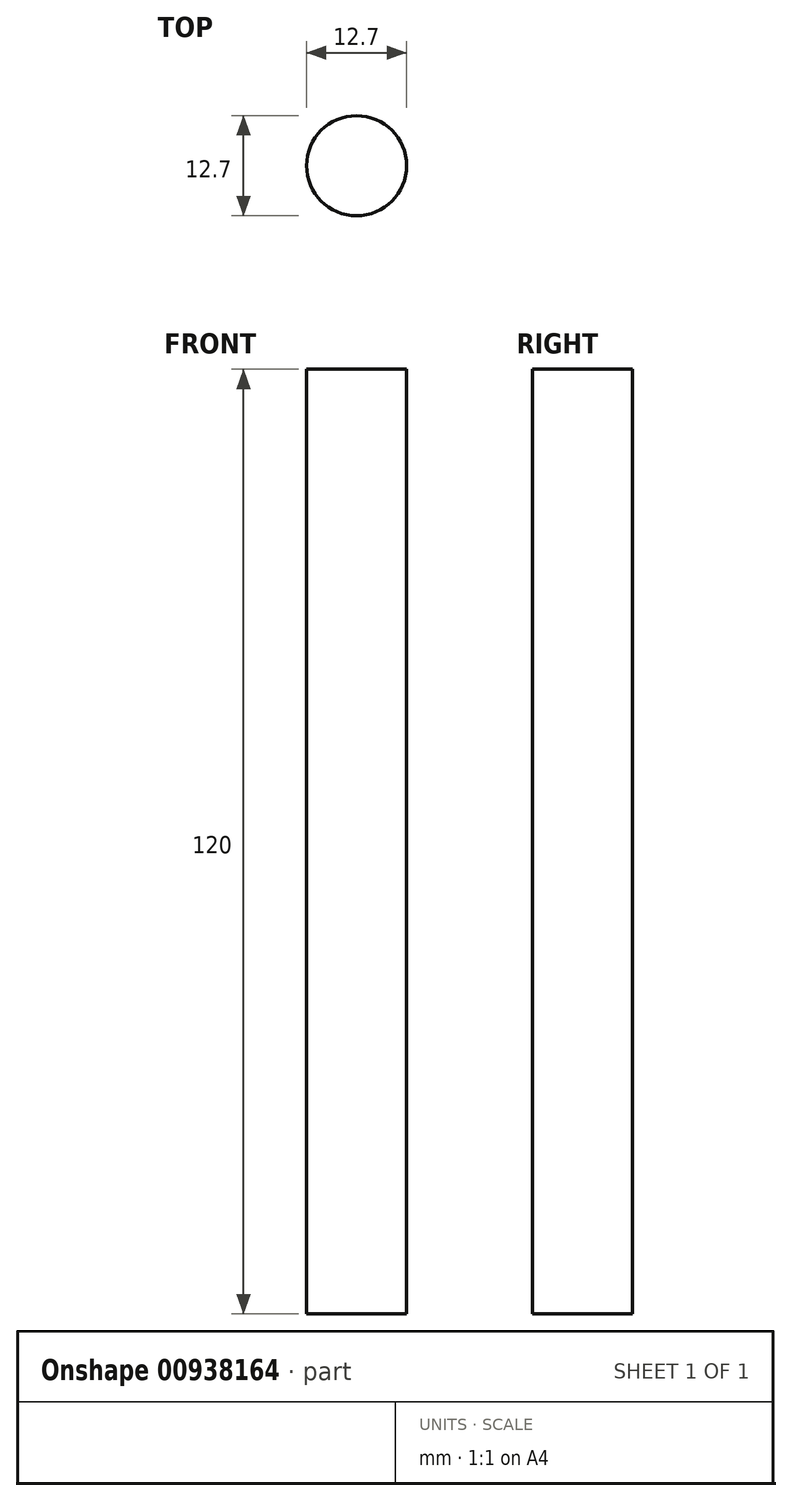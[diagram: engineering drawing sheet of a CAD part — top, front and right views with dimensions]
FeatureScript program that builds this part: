
annotation { "Feature Type Name" : "Feature", "Feature Type Description" : "" }
export const myFeature = defineFeature(function(context is Context, id is Id, definition is map)
    precondition{}
    {
        {
            var Q0;
            Q0=qCreatedBy(makeId("Top.planeOp"),FACE);
            var sketch = newSketch(context, id + "F0", { "sketchPlane" : qUnion([Q0])});
            skCircle(sketch, "E0", {"center": v(11.02, 41.68) * mm, "radius": 6.35 * mm});
            skSolve(sketch);
        }
        {
            var Q0;
            Q0=makeQuery(id+"F0.imprint","IMPRINT",FACE,{"disambiguationData":[TD([[makeQuery(id+"F0.imprint","IMPRINT",EDGE,{"derivedFrom":sQuery(id+"F0.wireOp",EDGE,"E0")}),1.0]])]});
            extrude(context, id + "F1", {"entities" : qUnion([Q0]), "depth" : 120 * mm, "offsetDistance" : 25 * mm});
        }
    });
